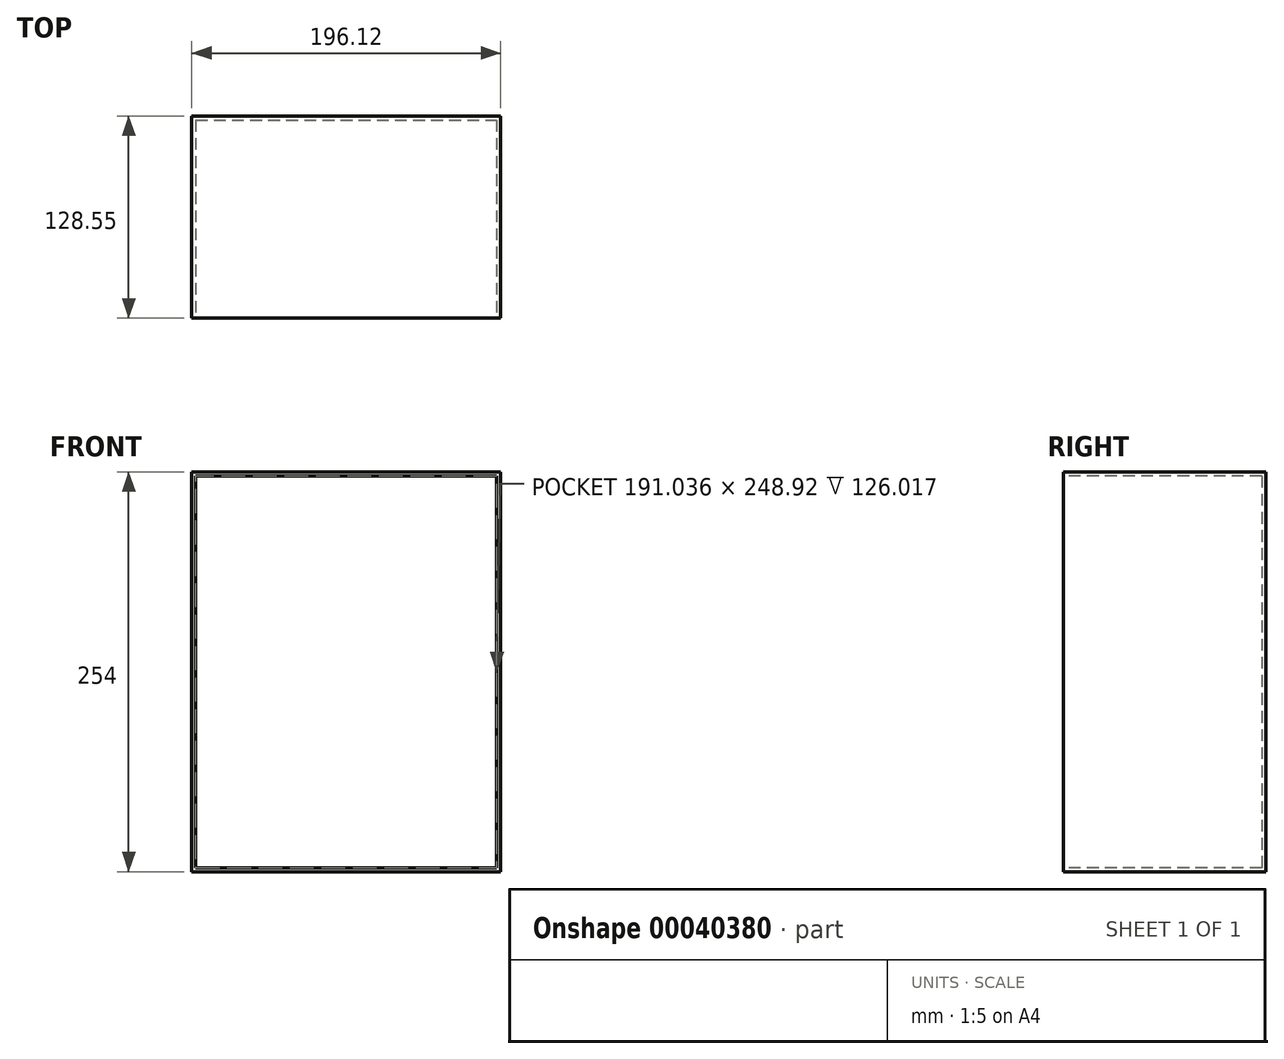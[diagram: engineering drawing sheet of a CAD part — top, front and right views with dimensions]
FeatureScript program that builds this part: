
annotation { "Feature Type Name" : "Feature", "Feature Type Description" : "" }
export const myFeature = defineFeature(function(context is Context, id is Id, definition is map)
    precondition{}
    {
        {
            var Q0;
            Q0=qCreatedBy(makeId("Top.planeOp"),FACE);
            var sketch = newSketch(context, id + "F0", { "sketchPlane" : qUnion([Q0])});
            skLineSegment(sketch, "E0.bottom", {"start": v(-91.1, 61.67) * mm, "end": v(105, 61.67) * mm});
            skLineSegment(sketch, "E0.top", {"start": v(-91.1, -66.88) * mm, "end": v(105, -66.88) * mm});
            skLineSegment(sketch, "E0.left", {"start": v(-91.1, 61.67) * mm, "end": v(-91.1, -66.88) * mm});
            skLineSegment(sketch, "E0.right", {"start": v(105, 61.67) * mm, "end": v(105, -66.88) * mm});
            skSolve(sketch);
        }
        {
            var Q0;
            Q0 = qSketchRegion(id + "F0", true);
            extrude(context, id + "F1", {"entities" : qUnion([Q0]), "depth" : 254 * mm});
        }
        {
            var Q0;
            Q0=makeQuery(id+"F1.opExtrude","SWEPT_FACE",FACE,{"disambiguationData":[OSD([sQuery(id+"F0.wireOp",EDGE,"E0.top")])]});
            shell(context, id + "F2", {"entities" : qUnion([Q0]), "thickness" : 2.54 * mm});
        }
    });
